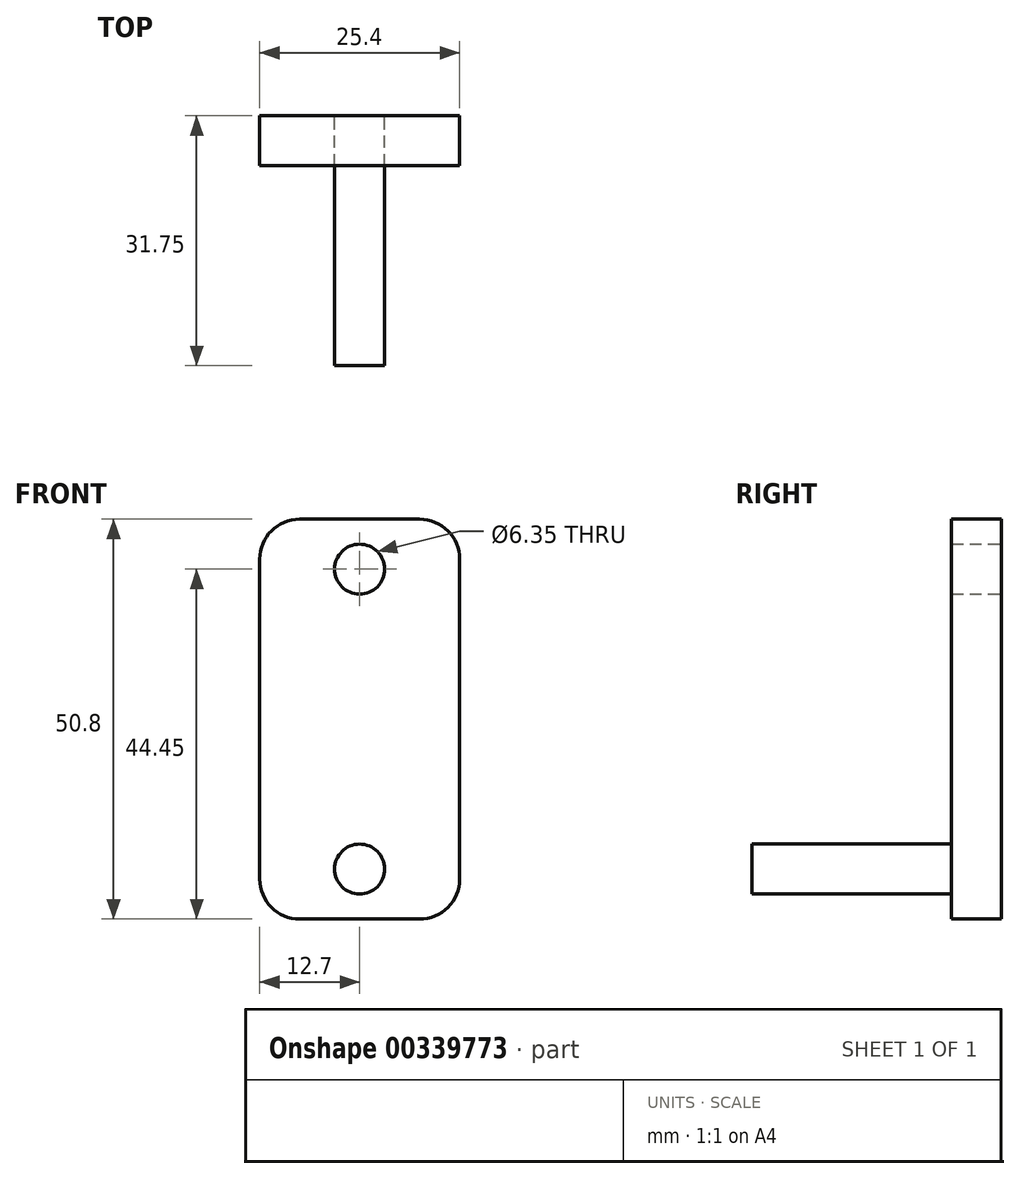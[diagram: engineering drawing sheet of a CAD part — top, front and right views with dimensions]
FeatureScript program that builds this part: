
annotation { "Feature Type Name" : "Feature", "Feature Type Description" : "" }
export const myFeature = defineFeature(function(context is Context, id is Id, definition is map)
    precondition{}
    {
        {
            var Q0;
            Q0=qCreatedBy(makeId("Front.planeOp"),FACE);
            var sketch = newSketch(context, id + "F0", { "sketchPlane" : qUnion([Q0])});
            skLineSegment(sketch, "E0.bottom", {"start": v(0, 0) * mm, "end": v(25.4, 0) * mm});
            skLineSegment(sketch, "E0.top", {"start": v(0, -50.8) * mm, "end": v(25.4, -50.8) * mm});
            skLineSegment(sketch, "E0.left", {"start": v(0, 0) * mm, "end": v(0, -50.8) * mm});
            skLineSegment(sketch, "E0.right", {"start": v(25.4, 0) * mm, "end": v(25.4, -50.8) * mm});
            skCircle(sketch, "E1", {"center": v(12.7, -6.35) * mm, "radius": 3.18 * mm});
            skSolve(sketch);
        }
        {
            var Q0;
            Q0=makeQuery(id+"F0.imprint","IMPRINT",FACE,{"disambiguationData":[TD([[makeQuery(id+"F0.imprint","IMPRINT",EDGE,{"derivedFrom":sQuery(id+"F0.wireOp",EDGE,"E0.bottom")}),-1.0]])]});
            extrude(context, id + "F1", {"entities" : qUnion([Q0]), "depth" : 6.35 * mm});
        }
        {
            var Q0;
            Q0=makeQuery(id+"F1.opExtrude","SWEPT_EDGE",EDGE,{"disambiguationData":[OSD([sQuery(id+"F0.wireOp",EDGE,"E0.bottom"),sQuery(id+"F0.wireOp",EDGE,"E0.left")])]});
            fillet(context, id + "F2", {"entities" : qUnion([Q0]), "radius" : 5.08 * mm, "tangentPropagation" : true, "allowEdgeOverflow" : false});
        }
        {
            var Q0;
            Q0=makeQuery(id+"F1.opExtrude","SWEPT_EDGE",EDGE,{"disambiguationData":[OSD([sQuery(id+"F0.wireOp",EDGE,"E0.bottom"),sQuery(id+"F0.wireOp",EDGE,"E0.right")])]});
            fillet(context, id + "F3", {"entities" : qUnion([Q0]), "radius" : 5.08 * mm, "tangentPropagation" : true, "allowEdgeOverflow" : false});
        }
        {
            var Q0;
            Q0=makeQuery(id+"F1.opExtrude","SWEPT_EDGE",EDGE,{"disambiguationData":[OSD([sQuery(id+"F0.wireOp",EDGE,"E0.top"),sQuery(id+"F0.wireOp",EDGE,"E0.right")])]});
            var Q1;
            Q1=makeQuery(id+"F1.opExtrude","SWEPT_EDGE",EDGE,{"disambiguationData":[OSD([sQuery(id+"F0.wireOp",EDGE,"E0.top"),sQuery(id+"F0.wireOp",EDGE,"E0.left")])]});
            fillet(context, id + "F4", {"entities" : qUnion([Q0, Q1]), "radius" : 5.08 * mm, "tangentPropagation" : true, "allowEdgeOverflow" : false});
        }
        {
            var Q0;
            Q0=makeQuery(id+"F1.opExtrude","CAP_FACE",FACE,{"disambiguationData":[OSD([sQuery(id+"F0.wireOp",EDGE,"E0.bottom"),sQuery(id+"F0.wireOp",EDGE,"E0.top"),sQuery(id+"F0.wireOp",EDGE,"E0.left"),sQuery(id+"F0.wireOp",EDGE,"E0.right"),sQuery(id+"F0.wireOp",EDGE,"E1")])],"isStart":false});
            var sketch = newSketch(context, id + "F5", { "sketchPlane" : qUnion([Q0])});
            skCircle(sketch, "E2", {"center": v(12.7, -44.45) * mm, "radius": 3.18 * mm});
            skSolve(sketch);
        }
        {
            var Q0;
            Q0=makeQuery(id+"F5.imprint","IMPRINT",FACE,{"disambiguationData":[TD([[makeQuery(id+"F5.imprint","IMPRINT",EDGE,{"derivedFrom":sQuery(id+"F5.wireOp",EDGE,"E2")}),1.0]])]});
            extrude(context, id + "F6", {"entities" : qUnion([Q0]), "operationType" : NewBodyOperationType.ADD, "depth" : 25.4 * mm});
        }
    });
